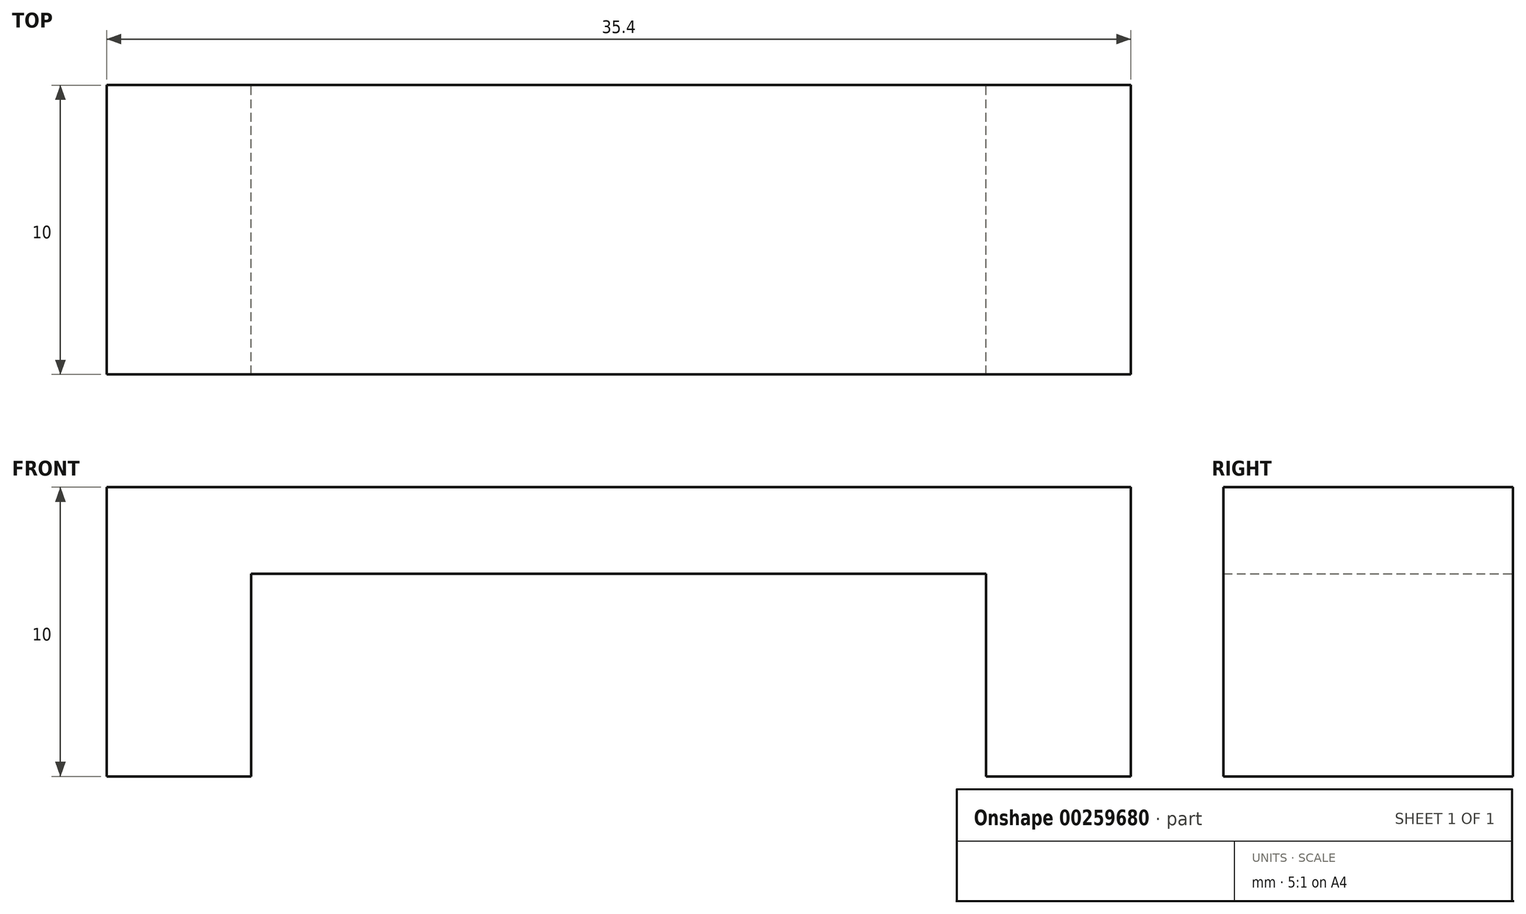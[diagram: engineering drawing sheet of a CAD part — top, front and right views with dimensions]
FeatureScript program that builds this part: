
annotation { "Feature Type Name" : "Feature", "Feature Type Description" : "" }
export const myFeature = defineFeature(function(context is Context, id is Id, definition is map)
    precondition{}
    {
        {
            var Q0;
            Q0=qCreatedBy(makeId("Top.planeOp"),FACE);
            var sketch = newSketch(context, id + "F0", { "sketchPlane" : qUnion([Q0])});
            skLineSegment(sketch, "E0.bottom", {"start": v(-17.7, -7.66) * mm, "end": v(-12.7, -7.66) * mm});
            skLineSegment(sketch, "E0.top", {"start": v(-17.7, -17.66) * mm, "end": v(-12.7, -17.66) * mm});
            skLineSegment(sketch, "E0.left", {"start": v(-17.7, -7.66) * mm, "end": v(-17.7, -17.66) * mm});
            skLineSegment(sketch, "E0.right", {"start": v(-12.7, -7.66) * mm, "end": v(-12.7, -17.66) * mm});
            skSolve(sketch);
        }
        {
            var Q0;
            Q0=makeQuery(id+"F0.imprint","IMPRINT",FACE,{"disambiguationData":[TD([[makeQuery(id+"F0.imprint","IMPRINT",EDGE,{"derivedFrom":sQuery(id+"F0.wireOp",EDGE,"E0.bottom")}),-1.0]])]});
            extrude(context, id + "F1", {"entities" : qUnion([Q0]), "depth" : 10 * mm});
        }
        {
            var Q0;
            Q0=makeQuery(id+"F1.opExtrude","SWEPT_FACE",FACE,{"disambiguationData":[OSD([sQuery(id+"F0.wireOp",EDGE,"E0.right")])]});
            var sketch = newSketch(context, id + "F2", { "sketchPlane" : qUnion([Q0])});
            skLineSegment(sketch, "E1.bottom", {"start": v(-17.66, 10) * mm, "end": v(-7.66, 10) * mm});
            skLineSegment(sketch, "E1.top", {"start": v(-17.66, 7) * mm, "end": v(-7.66, 7) * mm});
            skLineSegment(sketch, "E1.left", {"start": v(-17.66, 10) * mm, "end": v(-17.66, 7) * mm});
            skLineSegment(sketch, "E1.right", {"start": v(-7.66, 10) * mm, "end": v(-7.66, 7) * mm});
            skSolve(sketch);
        }
        {
            var Q0;
            Q0=makeQuery(id+"F2.imprint","IMPRINT",FACE,{"disambiguationData":[TD([[makeQuery(id+"F2.imprint","IMPRINT",EDGE,{"derivedFrom":sQuery(id+"F2.wireOp",EDGE,"E1.bottom")}),1.0]])]});
            var Q1;
            Q1=qCreatedBy(makeId("Right.planeOp"),FACE);
            extrude(context, id + "F3", {"entities" : qUnion([Q0]), "operationType" : NewBodyOperationType.ADD, "endBound" : BoundingType.UP_TO_SURFACE, "endBoundEntityFace" : qUnion([Q1]), "depth" : 25.4 * mm});
        }
        {
            var Q0;
            Q0=makeQuery(id+"F1.opExtrude","SWEPT_BODY",BODY,{"disambiguationData":[OSD([sQuery(id+"F0.wireOp",EDGE,"E0.bottom"),sQuery(id+"F0.wireOp",EDGE,"E0.top"),sQuery(id+"F0.wireOp",EDGE,"E0.left"),sQuery(id+"F0.wireOp",EDGE,"E0.right")])]});
            var Q1;
            Q1=qCreatedBy(makeId("Right.planeOp"),FACE);
            mirror(context, id + "F4", {"operationType" : NewBodyOperationType.ADD, "entities" : qUnion([Q0]), "mirrorPlane" : qUnion([Q1])});
        }
    });
